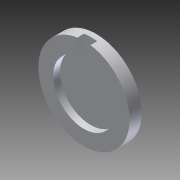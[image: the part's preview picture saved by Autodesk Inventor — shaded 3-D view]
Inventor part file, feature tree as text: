
AUTODESK INVENTOR PART (.ipt)
format: ipt  version: 2012 SP1 (Build 160190100, 190)  size: 90,624 bytes
history: native  units: in
note: dims shown in document units (in); Inventor stores cm internally (conversion verified against a paired STEP export)
features: extrude x2, sketch x2
ambient origin geometry x8: Origin, YZ Plane, XZ Plane, XY Plane, X Axis, Y Axis, Z Axis, Center Point
bodies: Solid1 (feature_tree)
feature tree (4):
  extrude  "Extrusion1"  Depth=0.156in TaperAngle=0.0deg
  extrude  "Extrusion2"  Depth=0.1673in
  sketch  "Sketch1"  dims[d0=1.17in d1=0.156in d2=0.0in]
  sketch  "Sketch2"  dims[d3=0.7874in d4=0.1673in d5=0.0869in d6=0.0in]
